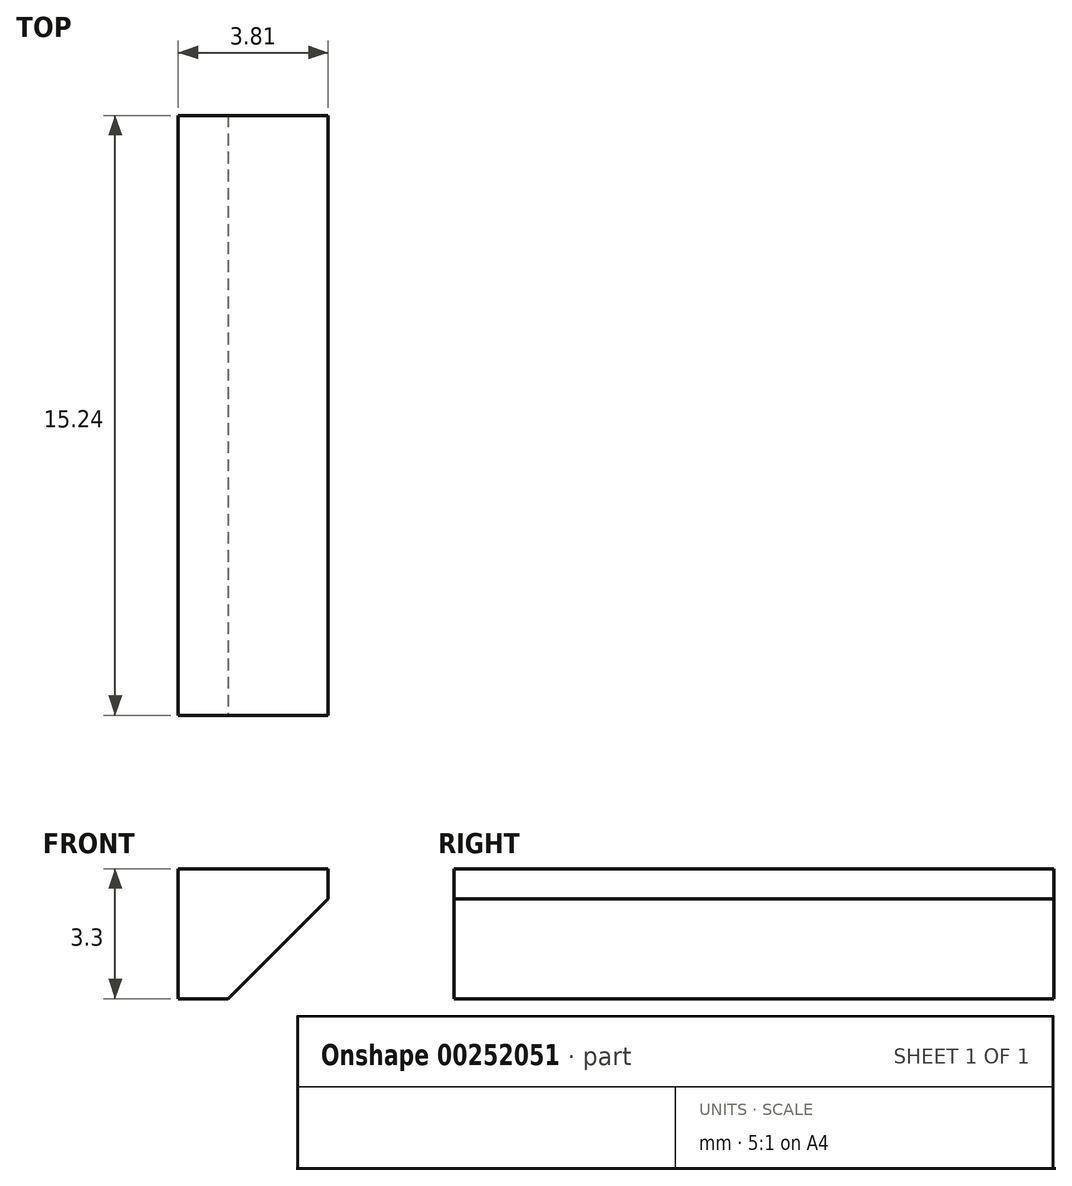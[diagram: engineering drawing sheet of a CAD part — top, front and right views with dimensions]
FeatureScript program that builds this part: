
annotation { "Feature Type Name" : "Feature", "Feature Type Description" : "" }
export const myFeature = defineFeature(function(context is Context, id is Id, definition is map)
    precondition{}
    {
        {
            var Q0;
            Q0=qCreatedBy(makeId("Right.planeOp"),FACE);
            var sketch = newSketch(context, id + "F0", { "sketchPlane" : qUnion([Q0])});
            skLineSegment(sketch, "E0.bottom", {"start": v(7.62, -5.13) * mm, "end": v(-7.62, -5.13) * mm});
            skLineSegment(sketch, "E0.top", {"start": v(7.62, -1.83) * mm, "end": v(-7.62, -1.83) * mm});
            skLineSegment(sketch, "E0.left", {"start": v(7.62, -5.13) * mm, "end": v(7.62, -1.83) * mm});
            skLineSegment(sketch, "E0.right", {"start": v(-7.62, -5.13) * mm, "end": v(-7.62, -1.83) * mm});
            skPoint(sketch, "E0.middle", {"position": v(0, -3.48) * mm});
            skSolve(sketch);
        }
        {
            var Q0;
            Q0 = qSketchRegion(id + "F0", true);
            extrude(context, id + "F1", {"entities" : qUnion([Q0]), "depth" : 3.8 * mm});
        }
        {
            var Q0;
            Q0=makeQuery(id+"F1.opExtrude","CAP_EDGE",EDGE,{"disambiguationData":[OSD([sQuery(id+"F0.wireOp",EDGE,"E0.bottom")])],"isStart":false});
            chamfer(context, id + "F2", {"entities" : qUnion([Q0]), "width" : 2.54 * mm, "tangentPropagation" : true});
        }
    });
